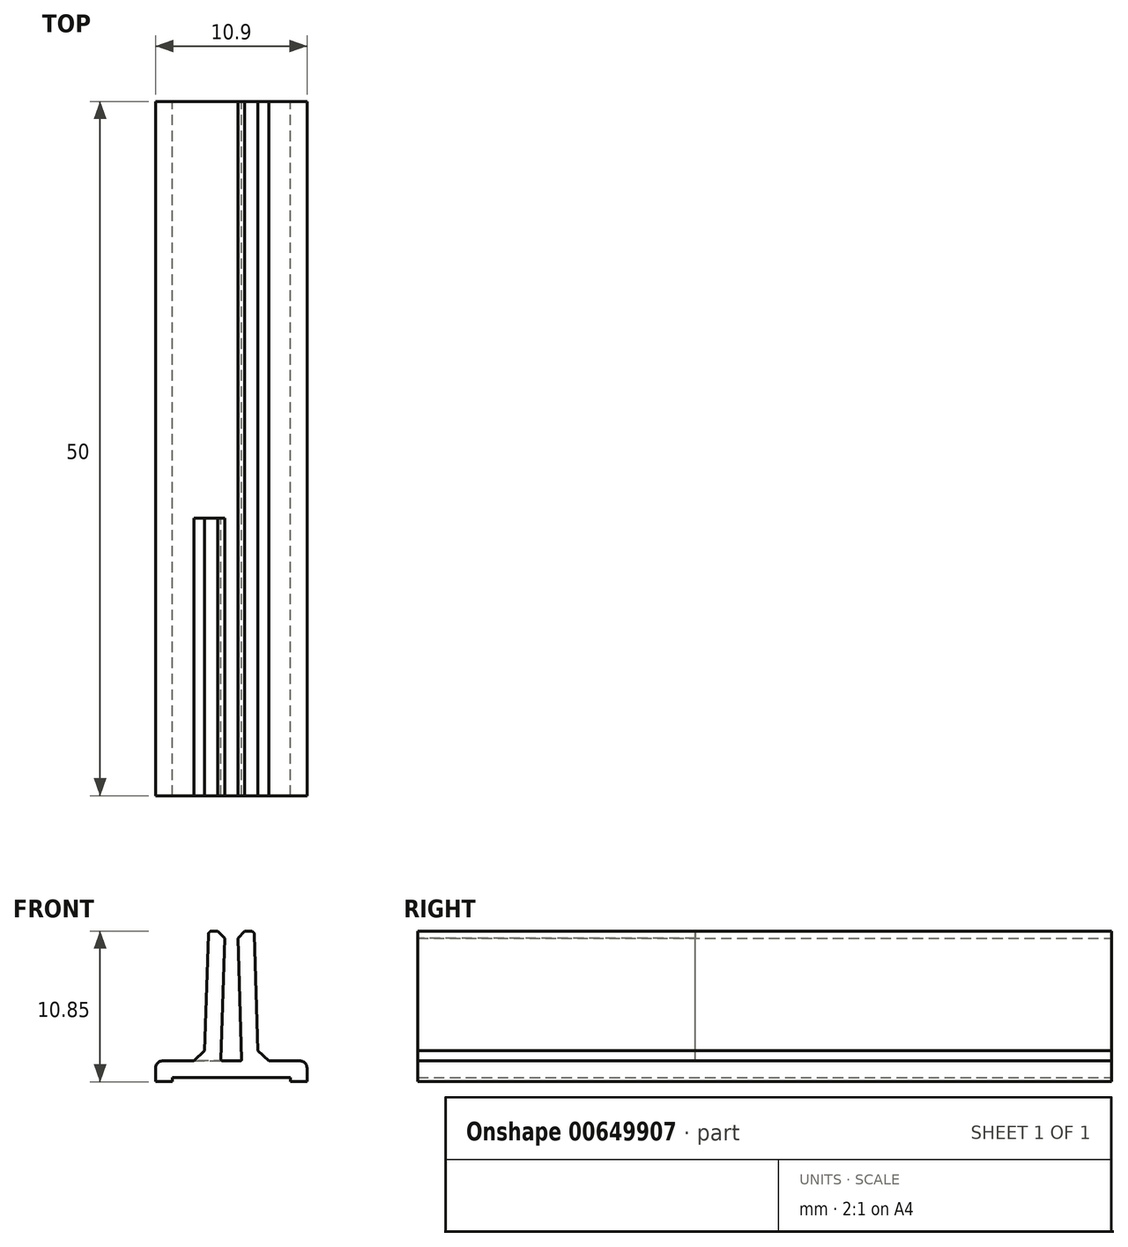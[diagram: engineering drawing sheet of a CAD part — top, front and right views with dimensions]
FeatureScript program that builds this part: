
annotation { "Feature Type Name" : "Feature", "Feature Type Description" : "" }
export const myFeature = defineFeature(function(context is Context, id is Id, definition is map)
    precondition{}
    {
        {
            var Q0;
            Q0=qCreatedBy(makeId("Front.planeOp"),FACE);
            var sketch = newSketch(context, id + "F0", { "sketchPlane" : qUnion([Q0])});
            skLineSegment(sketch, "E0.bottom", {"start": v(1.4, 5.75) * mm, "end": v(0.7, 5.75) * mm});
            skLineSegment(sketch, "E0.top", {"start": v(5.2, -5.1) * mm, "end": v(4.5, -5.1) * mm});
            skLineSegment(sketch, "E1", {"start": v(0, -3.6) * mm, "end": v(0.64, -3.6) * mm});
            skLineSegment(sketch, "E2", {"start": v(0.46, 5.5) * mm, "end": v(0.74, -3.5) * mm});
            skLineSegment(sketch, "E3", {"start": v(0.7, 5.75) * mm, "end": v(1.4, 5.75) * mm});
            skLineSegment(sketch, "E4", {"start": v(4.25, -4.8) * mm, "end": v(0, -4.8) * mm});
            skLineSegment(sketch, "E5", {"start": v(1.66, 5.5) * mm, "end": v(1.95, -3.6) * mm});
            skPoint(sketch, "E6.visualSharp", {"position": v(1.65, 5.75) * mm});
            skArc(sketch, "E6.filletArc", {"start": v(1.66, 5.5) * mm, "mid": v(1.58, 5.68) * mm, "end": v(1.4, 5.75) * mm});
            skPoint(sketch, "E7.visualSharp", {"position": v(1.95, -3.6) * mm});
            skPoint(sketch, "E8.visualSharp", {"position": v(0.75, -3.6) * mm});
            skArc(sketch, "E8.filletArc", {"start": v(0.64, -3.6) * mm, "mid": v(0.71, -3.56) * mm, "end": v(0.74, -3.5) * mm});
            skLineSegment(sketch, "E9", {"start": v(4.25, -4.8) * mm, "end": v(4.25, -5.1) * mm});
            skLineSegment(sketch, "E10", {"start": v(4.25, -5.1) * mm, "end": v(5.45, -5.1) * mm});
            skLineSegment(sketch, "E11", {"start": v(5.45, -5.1) * mm, "end": v(5.45, -4.85) * mm});
            skLineSegment(sketch, "E12", {"start": v(1.92, -2.85) * mm, "end": v(1.95, -3.6) * mm});
            skLineSegment(sketch, "E13", {"start": v(0.46, 5.5) * mm, "end": v(0.45, 5.74) * mm});
            skLineSegment(sketch, "E14", {"start": v(0.7, 5.75) * mm, "end": v(0.45, 5.74) * mm});
            skLineSegment(sketch, "E15", {"start": v(1.92, -2.85) * mm, "end": v(2.7, -3.6) * mm});
            skPoint(sketch, "E16.visualSharp", {"position": v(5.45, -3.6) * mm});
            skLineSegment(sketch, "E17", {"start": v(2.7, -3.6) * mm, "end": v(4.95, -3.6) * mm});
            skLineSegment(sketch, "E18", {"start": v(5.45, -5.1) * mm, "end": v(5.45, -4.1) * mm});
            skArc(sketch, "E19.filletArc", {"start": v(5.45, -4.1) * mm, "mid": v(5.3, -3.74) * mm, "end": v(4.95, -3.6) * mm});
            skLineSegment(sketch, "E20.MirrorCS", {"start": v(-0.46, 5.5) * mm, "end": v(-0.45, 5.74) * mm});
            skLineSegment(sketch, "E21.MirrorCS", {"start": v(-1.4, 5.75) * mm, "end": v(-0.7, 5.75) * mm});
            skLineSegment(sketch, "E22.MirrorCS", {"start": v(-0.7, 5.75) * mm, "end": v(-0.45, 5.74) * mm});
            skLineSegment(sketch, "E23.MirrorCS", {"start": v(-0.7, 5.75) * mm, "end": v(-1.4, 5.75) * mm});
            skArc(sketch, "E24.MirrorCS", {"start": v(-0.64, -3.6) * mm, "mid": v(-0.71, -3.56) * mm, "end": v(-0.74, -3.5) * mm});
            skLineSegment(sketch, "E25.MirrorCS", {"start": v(-1.92, -2.85) * mm, "end": v(-1.95, -3.6) * mm});
            skLineSegment(sketch, "E26.MirrorCS", {"start": v(-5.45, -5.1) * mm, "end": v(-5.45, -4.85) * mm});
            skArc(sketch, "E27.MirrorCS", {"start": v(-1.66, 5.5) * mm, "mid": v(-1.58, 5.68) * mm, "end": v(-1.4, 5.75) * mm});
            skLineSegment(sketch, "E28.MirrorCS", {"start": v(-5.2, -5.1) * mm, "end": v(-4.5, -5.1) * mm});
            skLineSegment(sketch, "E29.MirrorCS", {"start": v(-4.25, -4.8) * mm, "end": v(-4.25, -5.1) * mm});
            skLineSegment(sketch, "E30.MirrorCS", {"start": v(-1.92, -2.85) * mm, "end": v(-2.7, -3.6) * mm});
            skArc(sketch, "E31.MirrorCS", {"start": v(-5.45, -4.1) * mm, "mid": v(-5.3, -3.74) * mm, "end": v(-4.95, -3.6) * mm});
            skPoint(sketch, "E32.MirrorP", {"position": v(-5.45, -3.6) * mm});
            skLineSegment(sketch, "E33.MirrorCS", {"start": v(-4.25, -5.1) * mm, "end": v(-5.45, -5.1) * mm});
            skLineSegment(sketch, "E34.MirrorCS", {"start": v(-5.45, -5.1) * mm, "end": v(-5.45, -4.1) * mm});
            skLineSegment(sketch, "E35.MirrorCS", {"start": v(0, -3.6) * mm, "end": v(-0.64, -3.6) * mm});
            skPoint(sketch, "E36.MirrorP", {"position": v(-1.65, 5.75) * mm});
            skLineSegment(sketch, "E37.MirrorCS", {"start": v(-1.66, 5.5) * mm, "end": v(-1.95, -3.6) * mm});
            skPoint(sketch, "E38.MirrorP", {"position": v(-1.95, -3.6) * mm});
            skPoint(sketch, "E39.MirrorP", {"position": v(-0.75, -3.6) * mm});
            skLineSegment(sketch, "E40.MirrorCS", {"start": v(-4.25, -4.8) * mm, "end": v(0, -4.8) * mm});
            skLineSegment(sketch, "E41.MirrorCS", {"start": v(-2.7, -3.6) * mm, "end": v(-4.95, -3.6) * mm});
            skLineSegment(sketch, "E42.MirrorCS", {"start": v(-0.46, 5.5) * mm, "end": v(-0.74, -3.5) * mm});
            skSolve(sketch);
        }
        {
            var Q0;
            {var subQ4=sQuery(id+"F0.wireOp",EDGE,"E1");Q0=makeQuery(id+"F0.imprint","IMPRINT",FACE,{"disambiguationData":[TD([[makeQuery(id+"F0.imprint","IMPRINT",EDGE,{"derivedFrom":subQ4}),-1.0]])]});}
            extrude(context, id + "F1", {"entities" : qUnion([Q0]), "depth" : 50 * mm, "offsetDistance" : 25 * mm});
        }
        {
            var Q0;
            Q0=makeQuery(id+"F1.opExtrude","SWEPT_EDGE",EDGE,{"disambiguationData":[OSD([sQuery(id+"F0.wireOp",EDGE,"E20.MirrorCS"),sQuery(id+"F0.wireOp",EDGE,"E22.MirrorCS")])]});
            var Q1;
            Q1=makeQuery(id+"F1.opExtrude","SWEPT_EDGE",EDGE,{"disambiguationData":[OSD([sQuery(id+"F0.wireOp",EDGE,"E13"),sQuery(id+"F0.wireOp",EDGE,"E14")])]});
            chamfer(context, id + "F2", {"entities" : qUnion([Q0, Q1]), "width" : .5 * mm, "tangentPropagation" : true});
        }
        {
            var Q0;
            Q0=makeQuery(id+"F1.opExtrude","CAP_FACE",FACE,{"disambiguationData":[OSD([sQuery(id+"F0.wireOp",EDGE,"E1"),sQuery(id+"F0.wireOp",EDGE,"E2"),sQuery(id+"F0.wireOp",EDGE,"E3"),sQuery(id+"F0.wireOp",EDGE,"E4"),sQuery(id+"F0.wireOp",EDGE,"E5"),sQuery(id+"F0.wireOp",EDGE,"E6.filletArc"),sQuery(id+"F0.wireOp",EDGE,"E8.filletArc"),sQuery(id+"F0.wireOp",EDGE,"E9"),sQuery(id+"F0.wireOp",EDGE,"E10"),sQuery(id+"F0.wireOp",EDGE,"E13"),sQuery(id+"F0.wireOp",EDGE,"E14"),sQuery(id+"F0.wireOp",EDGE,"E15"),sQuery(id+"F0.wireOp",EDGE,"E17"),sQuery(id+"F0.wireOp",EDGE,"E18"),sQuery(id+"F0.wireOp",EDGE,"E19.filletArc"),sQuery(id+"F0.wireOp",EDGE,"E20.MirrorCS"),sQuery(id+"F0.wireOp",EDGE,"E22.MirrorCS"),sQuery(id+"F0.wireOp",EDGE,"E23.MirrorCS"),sQuery(id+"F0.wireOp",EDGE,"E24.MirrorCS"),sQuery(id+"F0.wireOp",EDGE,"E27.MirrorCS"),sQuery(id+"F0.wireOp",EDGE,"E29.MirrorCS"),sQuery(id+"F0.wireOp",EDGE,"E30.MirrorCS"),sQuery(id+"F0.wireOp",EDGE,"E31.MirrorCS"),sQuery(id+"F0.wireOp",EDGE,"E33.MirrorCS"),sQuery(id+"F0.wireOp",EDGE,"E34.MirrorCS"),sQuery(id+"F0.wireOp",EDGE,"E35.MirrorCS"),sQuery(id+"F0.wireOp",EDGE,"E37.MirrorCS"),sQuery(id+"F0.wireOp",EDGE,"E40.MirrorCS"),sQuery(id+"F0.wireOp",EDGE,"E41.MirrorCS"),sQuery(id+"F0.wireOp",EDGE,"E42.MirrorCS")])],"isStart":true});
            var sketch = newSketch(context, id + "F3", { "sketchPlane" : qUnion([Q0])});
            skLineSegment(sketch, "E43.0", {"start": v(0.64, -3.6) * mm, "end": v(-0.64, -3.6) * mm});
            skLineSegment(sketch, "E44.0", {"start": v(2.7, -3.6) * mm, "end": v(4.95, -3.6) * mm});
            skLineSegment(sketch, "E45", {"start": v(0, -3.6) * mm, "end": v(4.95, -3.6) * mm});
            skLineSegment(sketch, "E46", {"start": v(4.95, 6.1) * mm, "end": v(0, 6.1) * mm});
            skLineSegment(sketch, "E47", {"start": v(0, 6.1) * mm, "end": v(0, -3.6) * mm});
            skLineSegment(sketch, "E48", {"start": v(4.95, 6.1) * mm, "end": v(4.95, -3.6) * mm});
            skSolve(sketch);
        }
        {
            var Q0;
            Q0=qSketchRegion(id+"F3",true);
            extrude(context, id + "F4", {"entities" : qUnion([Q0]), "operationType" : NewBodyOperationType.REMOVE, "oppositeDirection" : true, "depth" : 30 * mm, "offsetDistance" : 25 * mm});
        }
    });
